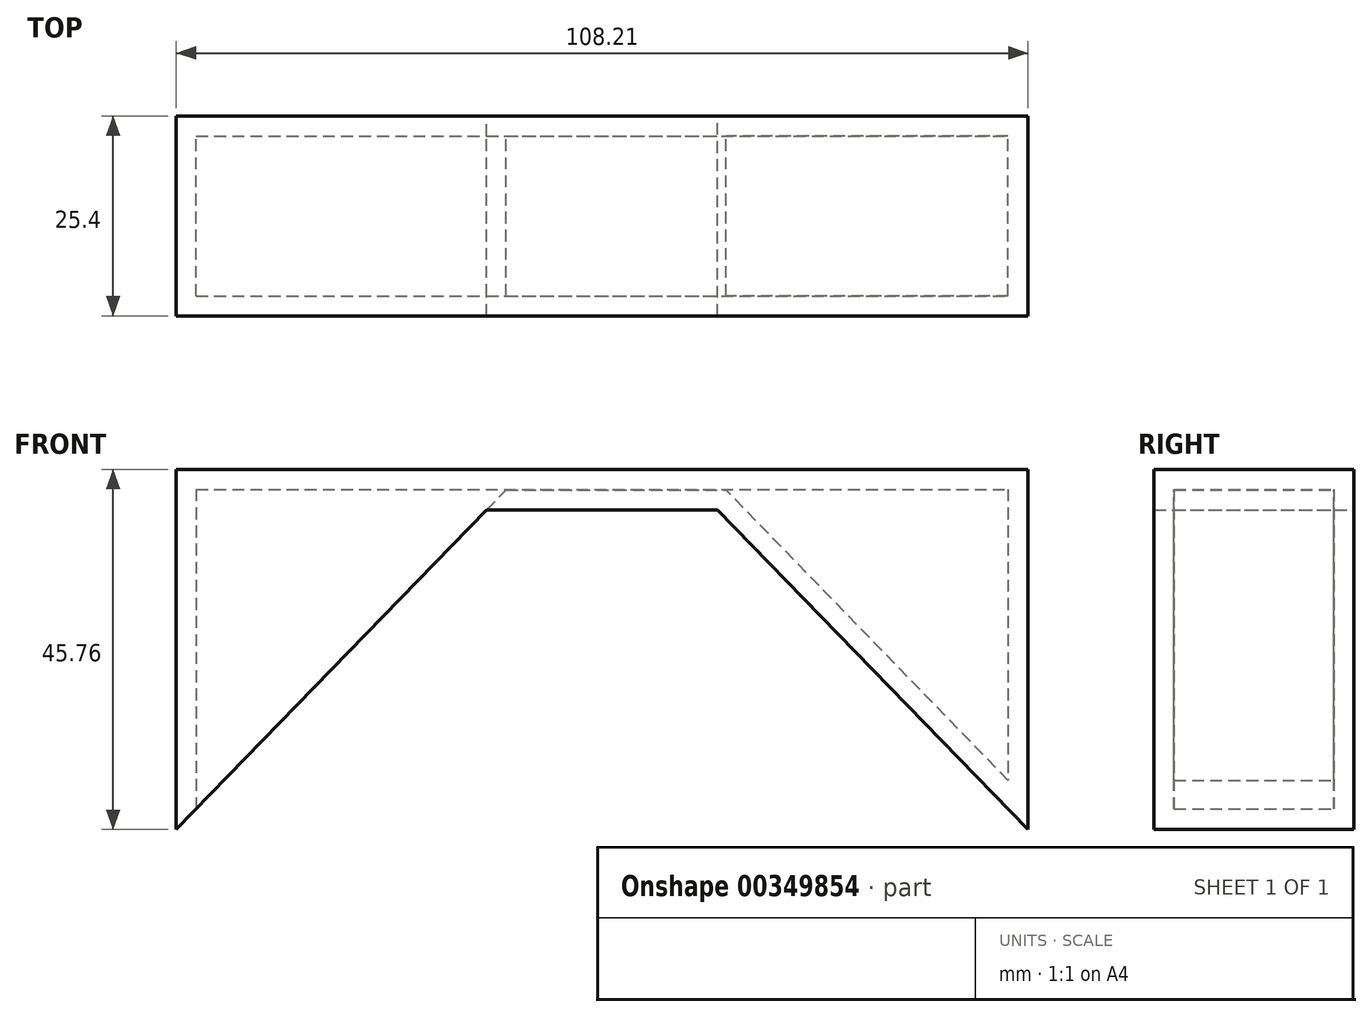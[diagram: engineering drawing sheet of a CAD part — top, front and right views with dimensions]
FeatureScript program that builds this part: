
annotation { "Feature Type Name" : "Feature", "Feature Type Description" : "" }
export const myFeature = defineFeature(function(context is Context, id is Id, definition is map)
    precondition{}
    {
        {
            var Q0;
            Q0=qCreatedBy(makeId("Front.planeOp"),FACE);
            var sketch = newSketch(context, id + "F0", { "sketchPlane" : qUnion([Q0])});
            skLineSegment(sketch, "E0", {"start": v(-55.83, 31.66) * mm, "end": v(52.38, 31.66) * mm});
            skLineSegment(sketch, "E1", {"start": v(52.38, 31.66) * mm, "end": v(52.38, -14.1) * mm});
            skLineSegment(sketch, "E2", {"start": v(-55.83, 31.66) * mm, "end": v(-55.83, -14.1) * mm});
            skLineSegment(sketch, "E3", {"start": v(-55.83, 26.48) * mm, "end": v(52.38, 26.48) * mm});
            skLineSegment(sketch, "E4", {"start": v(-55.83, -14.1) * mm, "end": v(-16.4, 26.48) * mm});
            skLineSegment(sketch, "E5", {"start": v(52.38, -14.1) * mm, "end": v(12.95, 26.48) * mm});
            skSolve(sketch);
        }
        {
            var Q0;
            {var subQ1=sQuery(id+"F0.wireOp",EDGE,"E0");Q0=makeQuery(id+"F0.imprint","IMPRINT",FACE,{"disambiguationData":[TD([[makeQuery(id+"F0.imprint","IMPRINT",EDGE,{"derivedFrom":subQ1}),-1.0]])]});}
            extrude(context, id + "F1", {"entities" : qUnion([Q0]), "depth" : 25.4 * mm});
        }
        {
            var Q0;
            Q0 = qSketchRegion(id + "F0", true);
            extrude(context, id + "F2", {"entities" : qUnion([Q0]), "operationType" : NewBodyOperationType.ADD, "depth" : 25.4 * mm});
        }
        {
            var Q0;
            Q0=makeQuery(id+"F2.opExtrude","SWEPT_FACE",FACE,{"disambiguationData":[OSD([sQuery(id+"F0.wireOp",EDGE,"E4")])]});
            shell(context, id + "F3", {"entities" : qUnion([Q0]), "thickness" : 2.54 * mm});
        }
    });
